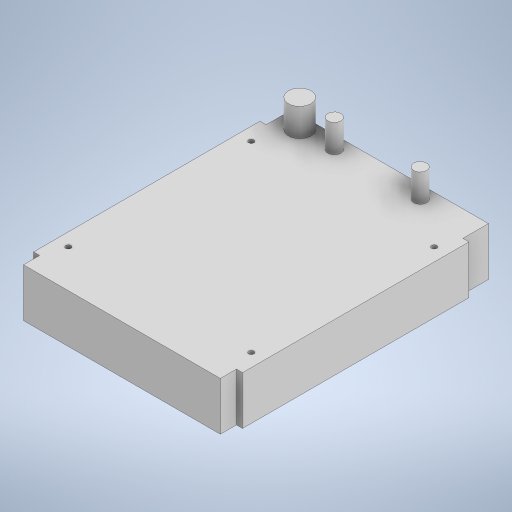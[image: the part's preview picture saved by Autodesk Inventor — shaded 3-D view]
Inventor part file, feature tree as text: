
AUTODESK INVENTOR PART (.ipt)
format: ipt  version: 2023 (Build 270158000, 158)  size: 242,688 bytes
history: native  units: mm
features: extrude x2, sketch x2
ambient origin geometry x8: Origin, YZ Plane, XZ Plane, XY Plane, X Axis, Y Axis, Z Axis, Center Point
bodies: Solid1 (feature_tree)
feature tree (4):
  extrude  "Extrusion1"  Depth=120.0mm
  extrude  "Extrusion2"  Depth=16.0mm
  sketch  "Sketch1"  dims[d0=130.0mm d1=120.0mm]
  sketch  "Sketch2"  dims[d2=105.0mm d3=3.048mm d4=14.7mm d5=113.0mm d6=9.25mm d7=27.75mm d8=0.0mm d9=13.0mm d10=7.5mm d11=12.0mm d12=31.85mm d13=31.85mm d14=16.0mm d15=0.0mm]
